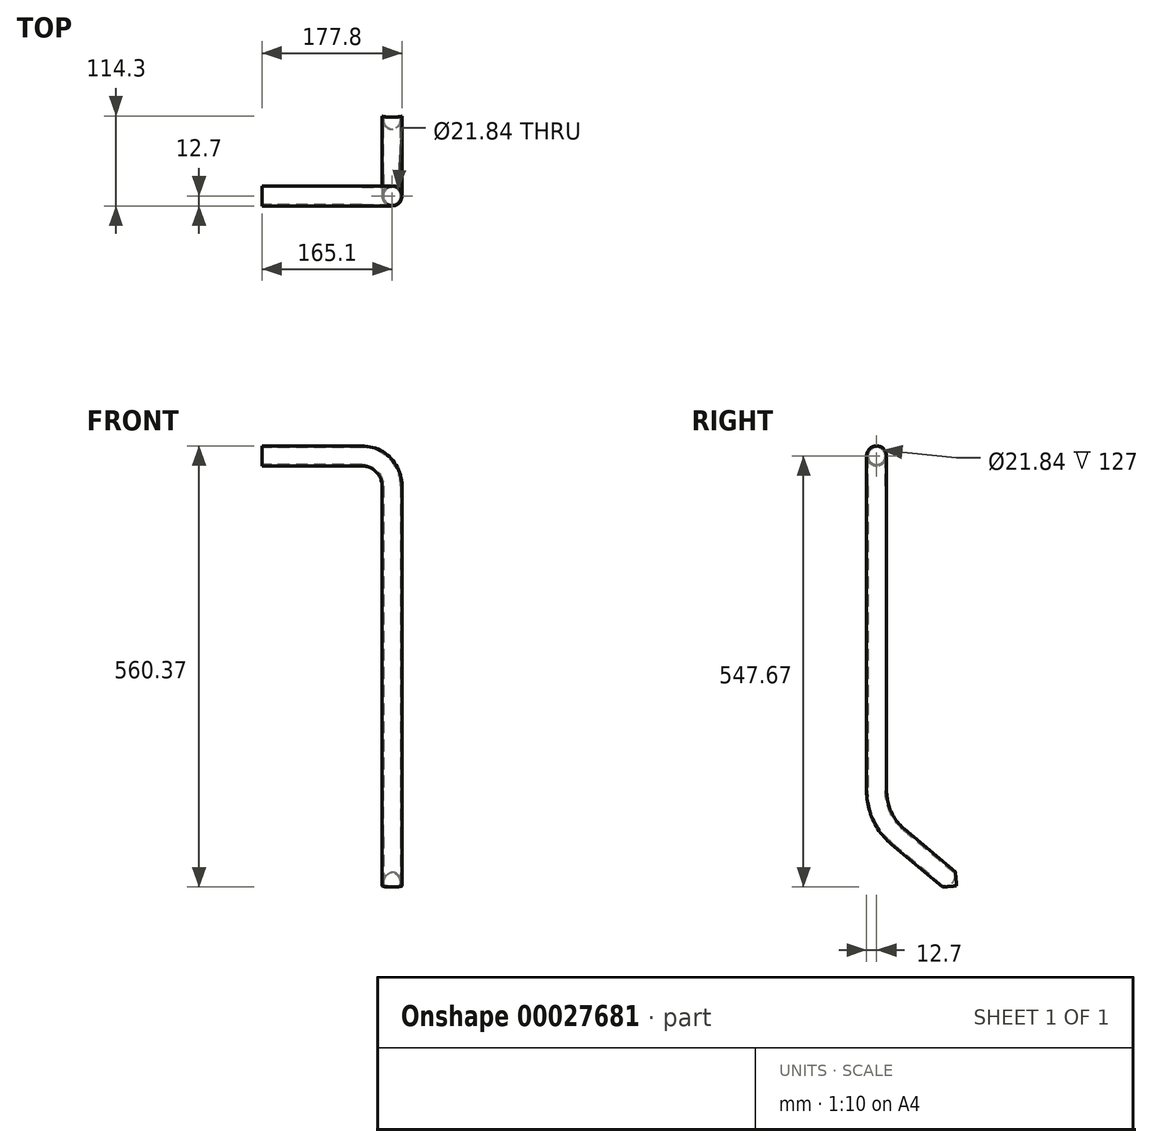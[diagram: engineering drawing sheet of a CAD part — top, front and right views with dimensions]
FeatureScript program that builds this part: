
annotation { "Feature Type Name" : "Feature", "Feature Type Description" : "" }
export const myFeature = defineFeature(function(context is Context, id is Id, definition is map)
    precondition{}
    {
        {
            var Q0;
            Q0=qCreatedBy(makeId("Right.planeOp"),FACE);
            var sketch = newSketch(context, id + "F0", { "sketchPlane" : qUnion([Q0])});
            skLineSegment(sketch, "E0", {"start": v(0, 0) * mm, "end": v(0, -336.41) * mm});
            skLineSegment(sketch, "E1", {"start": v(27.22, -394.79) * mm, "end": v(101.6, -457.2) * mm});
            skPoint(sketch, "E2.visualSharp", {"position": v(0, -371.95) * mm});
            skArc(sketch, "E2.filletArc", {"start": v(0, -336.41) * mm, "mid": v(7.14, -368.62) * mm, "end": v(27.22, -394.79) * mm});
            skSolve(sketch);
        }
        {
            var Q0;
            Q0=qCreatedBy(makeId("Top.planeOp"),FACE);
            var sketch = newSketch(context, id + "F1", { "sketchPlane" : qUnion([Q0])});
            skCircle(sketch, "E3", {"center": v(0, 0) * mm, "radius": 12.7 * mm});
            skCircle(sketch, "E4", {"center": v(0, 0) * mm, "radius": 10.92 * mm});
            skSolve(sketch);
        }
        {
            var Q0;
            Q0=qCreatedBy(makeId("Front.planeOp"),FACE);
            var sketch = newSketch(context, id + "F2", { "sketchPlane" : qUnion([Q0])});
            skLineSegment(sketch, "E5", {"start": v(0, 0) * mm, "end": v(0, 50.8) * mm});
            skLineSegment(sketch, "E6", {"start": v(-38.1, 88.9) * mm, "end": v(-165.1, 88.9) * mm});
            skPoint(sketch, "E7.visualSharp", {"position": v(0, 88.9) * mm});
            skArc(sketch, "E7.filletArc", {"start": v(0, 50.8) * mm, "mid": v(-11.16, 77.74) * mm, "end": v(-38.1, 88.9) * mm});
            skSolve(sketch);
        }
        {
            var Q0;
            Q0=makeQuery(id+"F1.imprint","IMPRINT",FACE,{"disambiguationData":[TD([[makeQuery(id+"F1.imprint","IMPRINT",EDGE,{"derivedFrom":sQuery(id+"F1.wireOp",EDGE,"E3")}),1.0]])]});
            var Q1;
            Q1=sQuery(id+"F0.wireOp",EDGE,"E0");
            var Q2;
            Q2=sQuery(id+"F0.wireOp",EDGE,"E2.filletArc");
            var Q3;
            Q3=sQuery(id+"F0.wireOp",EDGE,"E1");
            sweep(context, id + "F3", {"profiles" : qUnion([Q0]), "path" : qUnion([Q1, Q2, Q3])});
        }
        {
            var Q0;
            Q0=makeQuery(id+"F3.opSweep","CAP_FACE",FACE,{"disambiguationData":[OSD([sQuery(id+"F0.wireOp",VERTEX,"E0.start"),sQuery(id+"F1.wireOp",EDGE,"E3"),sQuery(id+"F1.wireOp",EDGE,"E4")])],"isStart":true});
            var Q1;
            Q1=sQuery(id+"F2.wireOp",EDGE,"E5");
            var Q2;
            Q2=sQuery(id+"F2.wireOp",EDGE,"1f83a44a-5fa5-4430-b063-b3ec6c71c0d4.filletArc");
            var Q3;
            Q3=sQuery(id+"F2.wireOp",EDGE,"QGguVBhc-vcTX-DwcB-YZOb-tXGgFPEWOa2z");
            var Q4;
            Q4=sQuery(id+"F2.wireOp",EDGE,"806b2ec1-c9d3-4610-b0db-3dc4d3c9ea74.filletArc");
            var Q5;
            Q5=sQuery(id+"F2.wireOp",EDGE,"a0jewLt4-rXq2-Rtom-dzgz-fkFbZhLJp1aM");
            sweep(context, id + "F4", {"operationType" : NewBodyOperationType.ADD, "profiles" : qUnion([Q0]), "path" : qUnion([Q1, Q2, Q3, Q4, Q5])});
        }
        {
            var Q0;
            Q0=sQuery(id+"F0.wireOp",EDGE,"E1");
            cPlane(context, id + "F5", {"entities" : qUnion([Q0]), "cplaneType" : CPlaneType.LINE_ANGLE, "offset" : 152.4 * mm, "angle" : 0 * degree, "width" : 152.4 * mm, "height" : 152.4 * mm});
        }
        {
            var Q0;
            Q0=qCreatedBy(id+"F5.planeOp",FACE);
            var sketch = newSketch(context, id + "F6", { "sketchPlane" : qUnion([Q0])});
            skLineSegment(sketch, "E8.0", {"start": v(12.7, 371.71) * mm, "end": v(-12.7, 371.71) * mm});
            skArc(sketch, "E9", {"start": v(-12.7, 371.71) * mm, "mid": v(0, 359.01) * mm, "end": v(12.7, 371.71) * mm});
            skSolve(sketch);
        }
        {
            var Q0;
            Q0 = qSketchRegion(id + "F6", true);
            extrude(context, id + "F7", {"entities" : qUnion([Q0]), "operationType" : NewBodyOperationType.REMOVE, "endBound" : BoundingType.THROUGH_ALL, "oppositeDirection" : true, "depth" : 25.4 * mm, "hasSecondDirection" : true, "secondDirectionBound" : BoundingType.THROUGH_ALL, "secondDirectionOppositeDirection" : false, "secondDirectionDepth" : 25.4 * mm});
        }
        {
            var Q0;
            Q0=makeQuery(id+"F4.opSweep","CAP_FACE",FACE,{"disambiguationData":[OSD([sQuery(id+"F0.wireOp",VERTEX,"E0.start"),sQuery(id+"F1.wireOp",EDGE,"E3"),sQuery(id+"F1.wireOp",EDGE,"E4"),sQuery(id+"F2.wireOp",VERTEX,"E5.end")])],"isStart":false});
            var Q1;
            Q1=sQuery(id+"F2.wireOp",EDGE,"E7.filletArc");
            var Q2;
            Q2=sQuery(id+"F2.wireOp",EDGE,"E6");
            var Q3;
            Q3=sQuery(id+"F2.wireOp",EDGE,"62dfd958-a358-41c3-8c18-c4489ac08ddc.filletArc");
            var Q4;
            Q4=sQuery(id+"F2.wireOp",EDGE,"6dOCTts8-fGJ9-YHF3-0bKr-Ga5cR4tcaJkH");
            sweep(context, id + "F8", {"operationType" : NewBodyOperationType.ADD, "profiles" : qUnion([Q0]), "path" : qUnion([Q1, Q2, Q3, Q4])});
        }
    });
